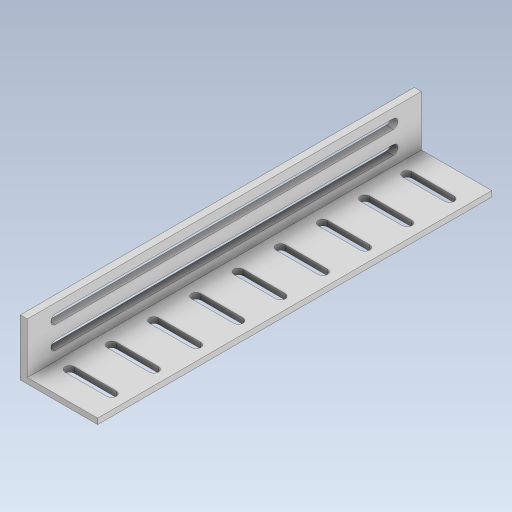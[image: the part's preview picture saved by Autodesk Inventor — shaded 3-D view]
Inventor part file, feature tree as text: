
AUTODESK INVENTOR PART (.ipt)
format: ipt  version: 2023.5 (Build 275446000, 446)  size: 210,944 bytes
history: native  units: mm
features: extrude x3, sketch x2
ambient origin geometry x8: Origin, YZ Plane, XZ Plane, XY Plane, X Axis, Y Axis, Z Axis, Center Point
bodies: Solid1 (feature_tree)
feature tree (5):
  sketch  "Sketch1"  dims[d0=27.5mm d1=140.0mm]
  extrude  "Extrusion1"  Depth=140.0mm
  extrude  "Extrusion2"  Depth=2.0mm TaperAngle=0.0deg
  extrude  "Extrusion3"  Depth=20.0mm TaperAngle=0.0deg
  sketch  "Sketch2"  dims[d2=2.5mm d3=2.0mm d4=0.0mm d5=20.0mm d6=0.0mm d7=3.3mm d8=5.0mm d9=3.3mm d10=5.0mm d11=10.0mm d12=10.0mm d15=3.3mm d16=3.3mm d17=2.5mm d18=0.0mm d19=120.0mm d20=120.0mm d21=3.3mm d22=10.0mm d23=5.0mm d24=3.3mm d25=5.0mm d26=90.0mm d28=15.0mm d29=10.0mm d31=10.0mm]
